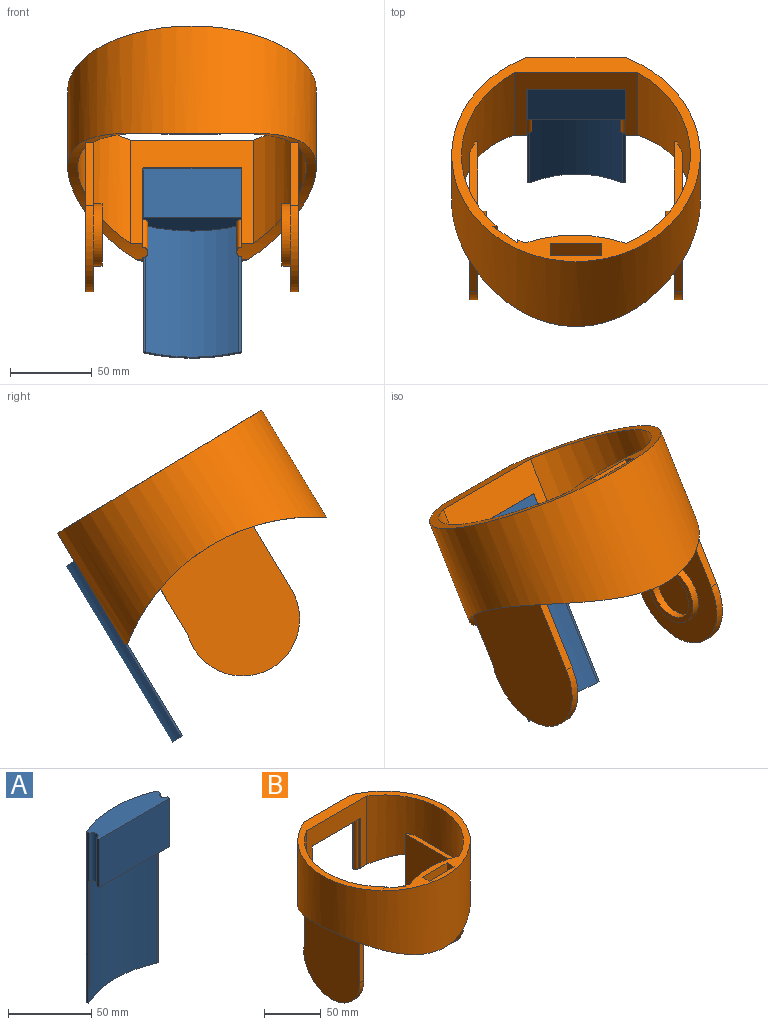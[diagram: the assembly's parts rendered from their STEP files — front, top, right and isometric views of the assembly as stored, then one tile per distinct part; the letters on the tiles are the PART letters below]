
ASSEMBLY  parts=2 mates=1
PART A: 16 faces, bbox 60x17x125.5 mm
  f0: plane 90x1.43mm, normal (0,-1,0), area 128.3mm2, adj f1,f7,f14,f15
  f1: plane 60x15.8mm, normal (0,0,-1), area 785.3mm2, adj f0,f2,f3,f4,f5,f6,f7,f9
  f2: cylinder r=2.97mm len=35.5mm, axis (0,0,-1), area 330.3mm2, adj f1,f3,f9,f10
  f3: plane 35.5x2.12mm, normal (-1,0,0), area 75.2mm2, adj f1,f2,f4,f10
  f4: plane 60x35.5mm, normal (0,-1,0), area 2130mm2, adj f1,f3,f5,f10
  f5: plane 35.5x2.12mm, normal (1,0,0), area 75.2mm2, adj f1,f4,f6,f10
  f6: cylinder r=2.7mm len=35.5mm, axis (0,0,-1), area 297.5mm2, adj f1,f5,f7,f10
  f7: plane 125.5x3.29mm, normal (1,0,0), area 241.2mm2, adj f0,f1,f6,f8,f10,f12,f15
  f8: cylinder r=76mm len=60mm, axis (0,0,-1), area 2189.6mm2, adj f7,f9,f10,f11
  f9: plane 125.5x2.76mm, normal (-1,0,0), area 222.4mm2, adj f1,f2,f8,f10,f12,f13,f15
  f10: plane 60x16.99mm, normal (0,0,1), area 873mm2, adj f2,f3,f4,f5,f6,f7,f8,f9
  f11: plane 60x6.17mm, normal (0,0,-1), area 3.2mm2, adj f8,f12
  f12: cylinder r=76.9mm len=90mm, axis (0,0,1), area 5547.3mm2, adj f7,f9,f11,f15
  f13: plane 90x1.6mm, normal (0,-1,0), area 144.4mm2, adj f1,f9,f14,f15
  f14: cylinder r=66.92mm len=90mm, axis (0,0,-1), area 5296.3mm2, adj f0,f1,f13,f15
  f15: plane 60x7.47mm, normal (0,0,-1), area 84.5mm2, adj f0,f7,f9,f12,f13,f14
PART B: 47 faces, bbox 152x145.8x138.2 mm
  f0: cylinder r=122.27mm len=152.01mm, axis (-1,0,0), area 2864.5mm2, adj f1,f2,f3,f4,f5,f6,f7,f8
  f1: cylinder r=70mm len=121.94mm, axis (0,0,-1), area 8722.7mm2, adj f0,f8,f9,f22,f37,f39,f40,f42
  f2: cylinder r=70mm len=109.74mm, axis (0,0,-1), area 7302.4mm2, adj f0,f8,f11,f22,f27,f28,f29,f31
  f3: plane 68.86x30.92mm, normal (0,-1,0), area 2129.3mm2, adj f0,f15,f21,f22
  f4: plane 73.89x30.92mm, normal (0,1,0), area 2284.7mm2, adj f0,f15,f21,f22
  f5: cylinder r=2.97mm len=59.22mm, axis (0,0,-1), area 531.3mm2, adj f0,f16,f20,f24,f26
  f6: cylinder r=76mm len=152mm, axis (0,0,-1), area 27196.3mm2, adj f0,f12,f13,f14,f16,f22,f23
  f7: cylinder r=2.7mm len=58.83mm, axis (0,0,-1), area 476.9mm2, adj f0,f14,f17,f24,f26
  f8: plane 75.3x73.68mm, normal (0,-1,0), area 2329.4mm2, adj f0,f1,f2,f17,f20,f22,f25
  f9: cylinder r=86.11mm len=68.8mm, axis (0,0,-1), area 4232.2mm2, adj f0,f1,f10,f22
  f10: cylinder r=70mm len=68.65mm, axis (0,0,-1), area 349.7mm2, adj f0,f9,f18,f22
  f11: plane 63.24x2.73mm, normal (0,-1,0), area 172.8mm2, adj f0,f2,f19,f22
  f12: plane 3.76x1.74mm, normal (0,0,-1), area 3.3mm2, adj f0,f6,f16
  f13: plane 3.76x1.74mm, normal (0,0,-1), area 3.3mm2, adj f0,f6,f14
  f14: plane 60x3.29mm, normal (-1,0,0), area 196.6mm2, adj f0,f6,f7,f13,f26
  f15: plane 73.89x8.69mm, normal (-1,0,0), area 619.3mm2, adj f0,f3,f4,f22
  f16: plane 60x2.76mm, normal (1,0,0), area 165.4mm2, adj f0,f5,f6,f12,f26
  f17: plane 55.02x2.12mm, normal (-1,0,0), area 115mm2, adj f0,f7,f8,f25
  f18: plane 68.65x2.46mm, normal (-1,0,0), area 167.5mm2, adj f0,f10,f19,f22
  f19: plane 68.65x15.2mm, normal (0.62,0.79,0), area 1270.5mm2, adj f0,f11,f18,f22
  f20: plane 55.02x2.12mm, normal (1,0,0), area 115mm2, adj f0,f5,f8,f25
  f21: plane 73.89x8.69mm, normal (1,0,0), area 619.3mm2, adj f0,f3,f4,f22
  f22: plane 152x145.83mm, normal (0,0,1), area 3308.8mm2, adj f1,f2,f3,f4,f6,f8,f9,f10
  f23: plane 60x20mm, normal (0,1,0), area 1200mm2, adj f6,f22,f26
  f24: plane 60x0.03mm, normal (0,1,0), area 1.7mm2, adj f5,f7,f25,f26
  f25: plane 60x2.12mm, normal (0,0,-1), area 127mm2, adj f8,f17,f20,f24
  f26: plane 60x8.7mm, normal (0,0,-1), area 497.1mm2, adj f5,f7,f14,f16,f23,f24
  f27: plane 68.51x5mm, normal (0,0,1), area 311.5mm2, adj f2,f28,f29,f31,f32
  f28: plane 98.56x69.72mm, normal (-1,0,0), area 5965.4mm2, adj f0,f2,f27,f29,f30,f31
  f29: plane 63.7x5mm, normal (0,-1,0), area 238.5mm2, adj f0,f2,f27,f28,f30,f32
  f30: cylinder r=34.86mm len=69.72mm, axis (-1,0,0), area 593.7mm2, adj f28,f29,f31,f32
  f31: plane 54.6x5mm, normal (0,1,0), area 193.8mm2, adj f0,f2,f27,f28,f30,f32
  f32: plane 98.56x69.72mm, normal (1,0,0), area 5123.3mm2, adj f27,f29,f30,f31,f34
  f33: cylinder r=15.61mm len=31.22mm, axis (-1,0,0), area 490.5mm2, adj f35,f36
  f34: cylinder r=19.2mm len=38.39mm, axis (-1,0,0), area 603mm2, adj f32,f35
  f35: plane 38.39x38.39mm, normal (1,0,0), area 391.8mm2, adj f33,f34
  f36: plane 31.22x31.22mm, normal (1,0,0), area 765.7mm2, adj f33
  f37: plane 68.51x5mm, normal (0,0,1), area 311.5mm2, adj f1,f39,f40,f41,f42
  f38: cylinder r=34.86mm len=69.72mm, axis (1,0,0), area 593.7mm2, adj f39,f40,f41,f42
  f39: plane 54.6x5mm, normal (0,1,0), area 193.8mm2, adj f0,f1,f37,f38,f41,f42
  f40: plane 63.7x5mm, normal (0,-1,0), area 238.5mm2, adj f0,f1,f37,f38,f41,f42
  f41: plane 98.56x69.72mm, normal (-1,0,0), area 5123.3mm2, adj f37,f38,f39,f40,f44
  f42: plane 98.56x69.72mm, normal (1,0,0), area 5965.4mm2, adj f0,f1,f37,f38,f39,f40
  f43: cylinder r=15.61mm len=31.22mm, axis (1,0,0), area 490.5mm2, adj f45,f46
  f44: cylinder r=19.2mm len=38.39mm, axis (1,0,0), area 603mm2, adj f41,f45
  f45: plane 38.39x38.39mm, normal (-1,0,0), area 391.8mm2, adj f43,f44
  f46: plane 31.22x31.22mm, normal (-1,0,0), area 765.7mm2, adj f43
PLACE A rot(axis=(-1,0,0),31.1deg) t=(25.23,-16.25,31.7)mm
PLACE B rot(axis=(-1,0,0),31.1deg) t=(25.16,-16.4,31.21)mm
MATE fastened A.f10 <-> B.f26  axis (0,0.52,0.86) through (25.31,57.81,27.33)mm
